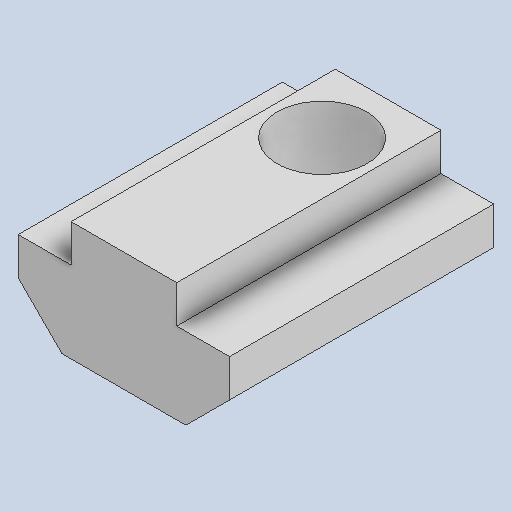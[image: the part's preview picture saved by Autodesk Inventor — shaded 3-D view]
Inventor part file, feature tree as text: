
AUTODESK INVENTOR PART (.ipt)
format: ipt  version: 2022 (Build 260153000, 153)  size: 109,568 bytes
history: native  units: in
note: dims shown in document units (in); Inventor stores cm internally (conversion verified against a paired STEP export)
features: fillet x1
ambient origin geometry x8: Origin, YZ Plane, XZ Plane, XY Plane, X Axis, Y Axis, Z Axis, Center Point
bodies: Solid1 (feature_tree)
feature tree (1):
  fillet  "Fillet1"  [1 undecoded]
note: 1 required parameter value undecoded (feature->parameter linkage not recoverable at this tier; creation-order binding heuristic only, values carry confidence <= 0.55)
